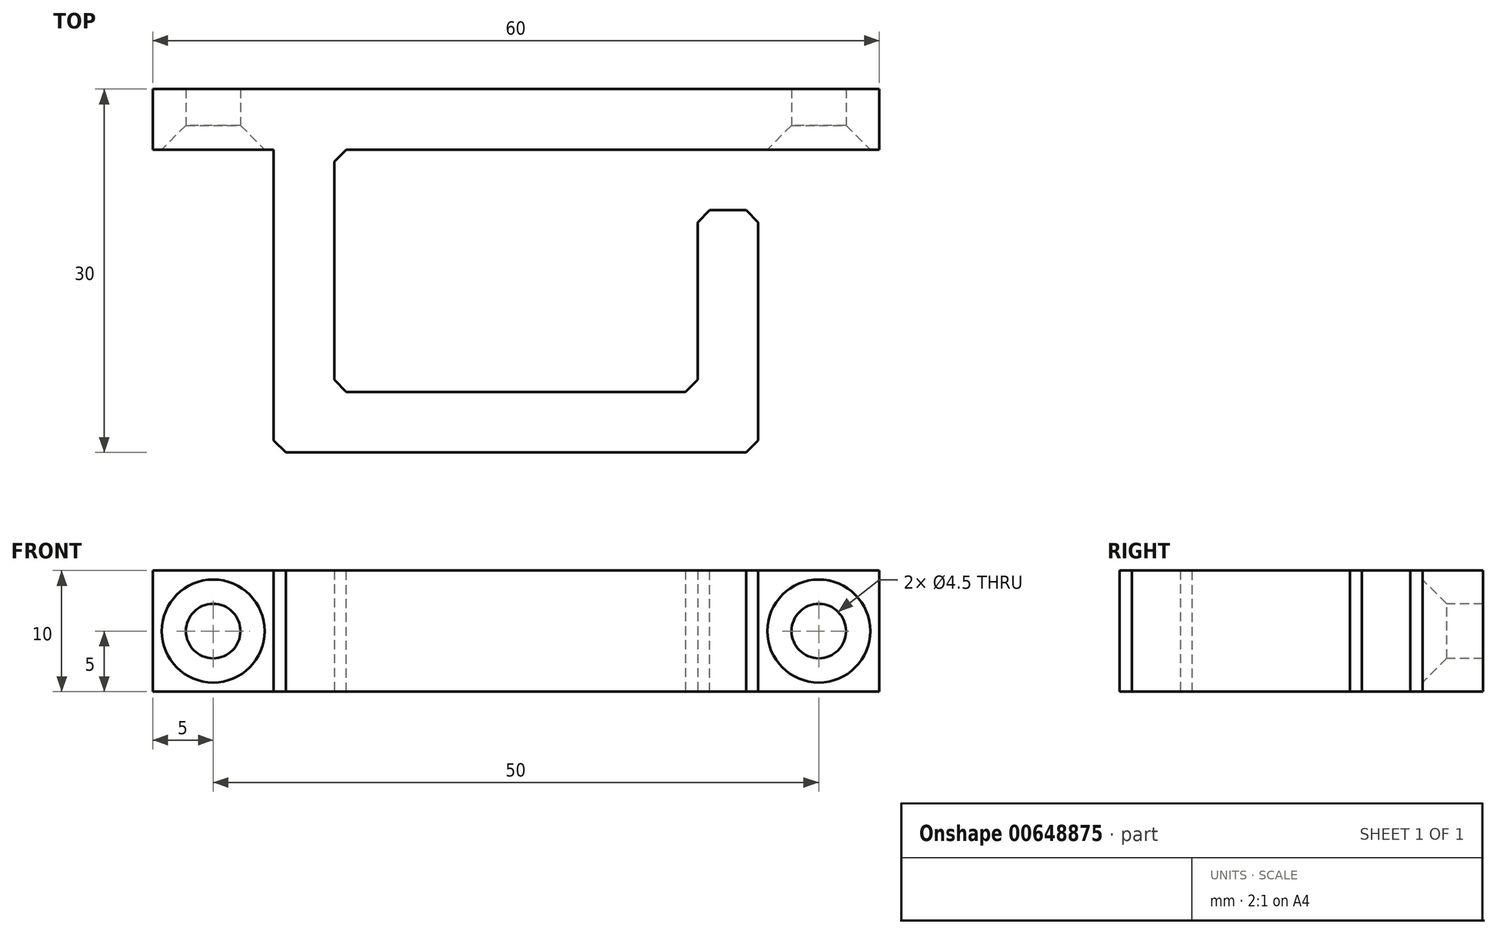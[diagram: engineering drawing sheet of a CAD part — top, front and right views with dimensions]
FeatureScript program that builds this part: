
annotation { "Feature Type Name" : "Feature", "Feature Type Description" : "" }
export const myFeature = defineFeature(function(context is Context, id is Id, definition is map)
    precondition{}
    {
        {
            var Q0;
            Q0=qCreatedBy(makeId("Top.planeOp"),FACE);
            var sketch = newSketch(context, id + "F0", { "sketchPlane" : qUnion([Q0])});
            skLineSegment(sketch, "E0", {"start": v(0, 0) * mm, "end": v(60, 0) * mm});
            skLineSegment(sketch, "E1", {"start": v(60, 0) * mm, "end": v(60, -5) * mm});
            skLineSegment(sketch, "E2", {"start": v(0, 0) * mm, "end": v(0, -5) * mm});
            skLineSegment(sketch, "E3", {"start": v(0, -5) * mm, "end": v(10, -5) * mm});
            skLineSegment(sketch, "E4", {"start": v(10, -5) * mm, "end": v(10, -30) * mm});
            skLineSegment(sketch, "E5", {"start": v(10, -30) * mm, "end": v(50, -30) * mm});
            skLineSegment(sketch, "E6", {"start": v(45, -25) * mm, "end": v(15, -25) * mm});
            skLineSegment(sketch, "E7", {"start": v(15, -25) * mm, "end": v(15, -5) * mm});
            skLineSegment(sketch, "E8", {"start": v(50, -30) * mm, "end": v(50, -10) * mm});
            skLineSegment(sketch, "E9", {"start": v(50, -10) * mm, "end": v(45, -10) * mm});
            skLineSegment(sketch, "E10", {"start": v(45, -10) * mm, "end": v(45, -25) * mm});
            skLineSegment(sketch, "E11", {"start": v(60, -5) * mm, "end": v(15, -5) * mm});
            skSolve(sketch);
        }
        {
            var Q0;
            Q0=makeQuery(id+"F0.imprint","IMPRINT",FACE,{"disambiguationData":[TD([[makeQuery(id+"F0.imprint","IMPRINT",EDGE,{"derivedFrom":sQuery(id+"F0.wireOp",EDGE,"E0")}),-1.0]])]});
            extrude(context, id + "F1", {"entities" : qUnion([Q0]), "depth" : 10 * mm, "offsetDistance" : 25 * mm});
        }
        {
            var Q0;
            Q0=makeQuery(id+"F1.opExtrude","SWEPT_FACE",FACE,{"disambiguationData":[OSD([sQuery(id+"F0.wireOp",EDGE,"E3")])]});
            var sketch = newSketch(context, id + "F2", { "sketchPlane" : qUnion([Q0])});
            skPoint(sketch, "E12.0", {"position": v(0, 10) * mm});
            skPoint(sketch, "E13", {"position": v(5, 5) * mm});
            skPoint(sketch, "E14.0", {"position": v(60, 10) * mm});
            skPoint(sketch, "E15", {"position": v(55, 5) * mm});
            skSolve(sketch);
        }
        {
            var Q0;
            Q0=sQuery(id+"F2.wireOp",VERTEX,"E13");
            var Q1;
            Q1=sQuery(id+"F2.wireOp",VERTEX,"E15");
            var Q2;
            Q2=makeQuery(id+"F1.opExtrude","SWEPT_BODY",BODY,{"disambiguationData":[OSD([sQuery(id+"F0.wireOp",EDGE,"E0"),sQuery(id+"F0.wireOp",EDGE,"E1"),sQuery(id+"F0.wireOp",EDGE,"E2"),sQuery(id+"F0.wireOp",EDGE,"E3"),sQuery(id+"F0.wireOp",EDGE,"E4"),sQuery(id+"F0.wireOp",EDGE,"E5"),sQuery(id+"F0.wireOp",EDGE,"E6"),sQuery(id+"F0.wireOp",EDGE,"E7"),sQuery(id+"F0.wireOp",EDGE,"E8"),sQuery(id+"F0.wireOp",EDGE,"E9"),sQuery(id+"F0.wireOp",EDGE,"E10"),sQuery(id+"F0.wireOp",EDGE,"E11")])]});
            hole(context, id + "F3", {"style" : HoleStyle.C_SINK, "endStyle" : HoleEndStyle.THROUGH, "holeDiameter" : 4.5 * mm, "cSinkDiameter" : 8.5 * mm, "cSinkAngle" : 90 * degree, "majorDiameter" : 3 * mm, "isTappedThrough" : true, "tappedDepth" : 12 * mm, "tapClearance" : 3, "startFromSketch" : true, "locations" : qUnion([Q0, Q1]), "scope" : qUnion([Q2])});
        }
        {
            var Q0;
            Q0=makeQuery(id+"F1.opExtrude","SWEPT_EDGE",EDGE,{"disambiguationData":[OSD([sQuery(id+"F0.wireOp",EDGE,"E8"),sQuery(id+"F0.wireOp",EDGE,"E9")])]});
            var Q1;
            Q1=makeQuery(id+"F1.opExtrude","SWEPT_EDGE",EDGE,{"disambiguationData":[OSD([sQuery(id+"F0.wireOp",EDGE,"E9"),sQuery(id+"F0.wireOp",EDGE,"E10")])]});
            var Q2;
            Q2=makeQuery(id+"F1.opExtrude","SWEPT_EDGE",EDGE,{"disambiguationData":[OSD([sQuery(id+"F0.wireOp",EDGE,"E7"),sQuery(id+"F0.wireOp",EDGE,"E11")])]});
            var Q3;
            Q3=makeQuery(id+"F1.opExtrude","SWEPT_EDGE",EDGE,{"disambiguationData":[OSD([sQuery(id+"F0.wireOp",EDGE,"E6"),sQuery(id+"F0.wireOp",EDGE,"E7")])]});
            var Q4;
            Q4=makeQuery(id+"F1.opExtrude","SWEPT_EDGE",EDGE,{"disambiguationData":[OSD([sQuery(id+"F0.wireOp",EDGE,"E6"),sQuery(id+"F0.wireOp",EDGE,"E10")])]});
            var Q5;
            Q5=makeQuery(id+"F1.opExtrude","SWEPT_EDGE",EDGE,{"disambiguationData":[OSD([sQuery(id+"F0.wireOp",EDGE,"E5"),sQuery(id+"F0.wireOp",EDGE,"E8")])]});
            var Q6;
            Q6=makeQuery(id+"F1.opExtrude","SWEPT_EDGE",EDGE,{"disambiguationData":[OSD([sQuery(id+"F0.wireOp",EDGE,"E4"),sQuery(id+"F0.wireOp",EDGE,"E5")])]});
            chamfer(context, id + "F4", {"entities" : qUnion([Q0, Q1, Q2, Q3, Q4, Q5, Q6]), "width" : 1 * mm, "tangentPropagation" : true});
        }
    });
